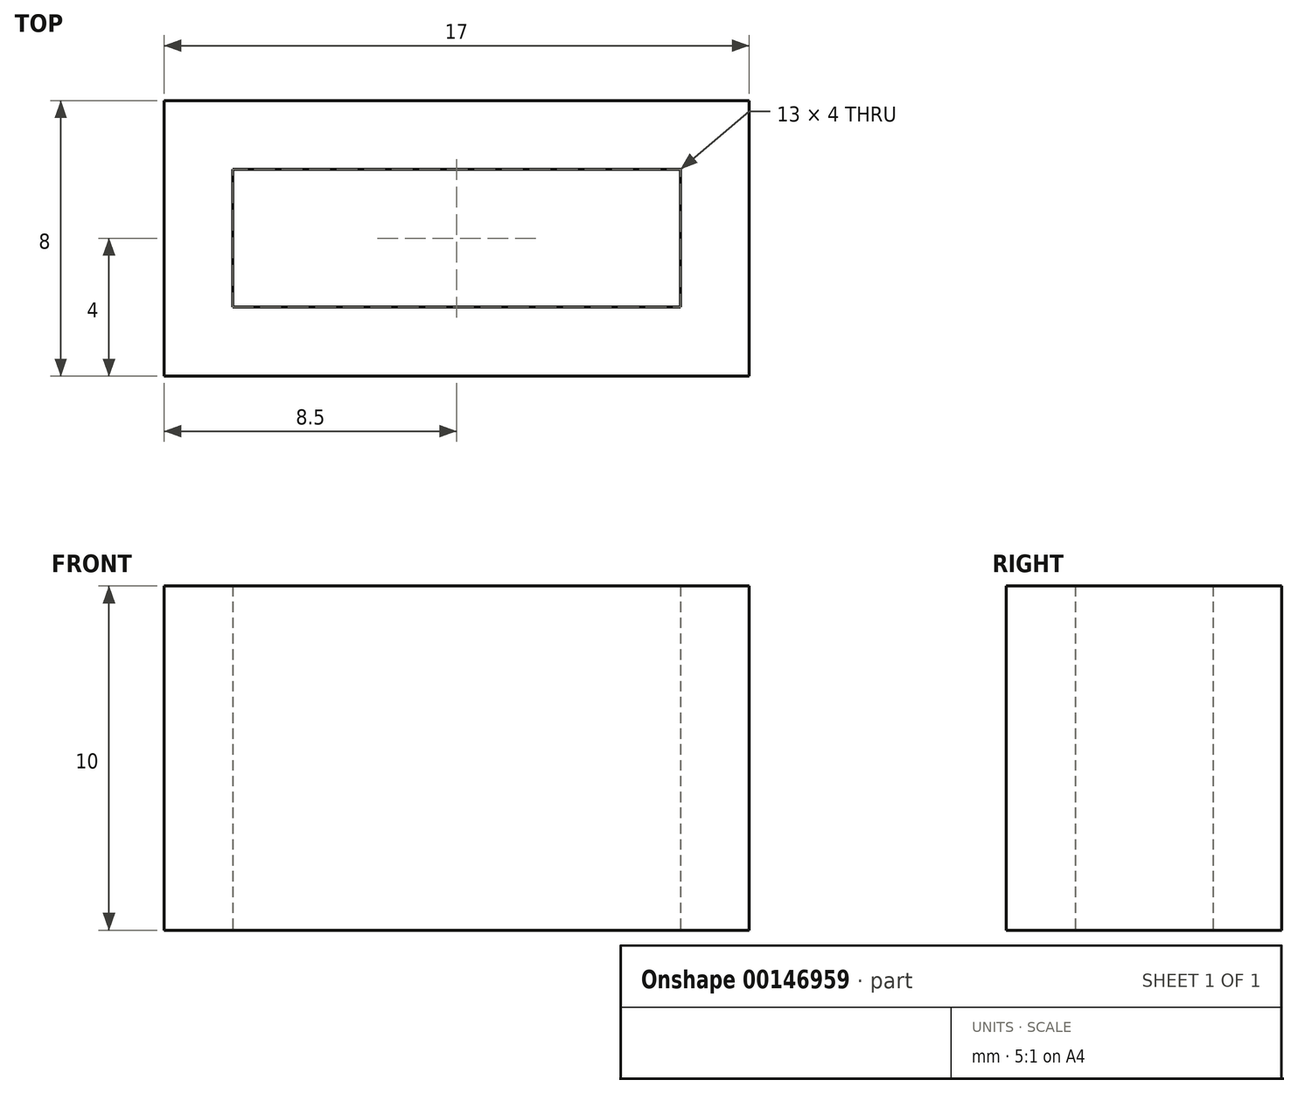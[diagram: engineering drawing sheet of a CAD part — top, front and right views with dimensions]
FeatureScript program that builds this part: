
annotation { "Feature Type Name" : "Feature", "Feature Type Description" : "" }
export const myFeature = defineFeature(function(context is Context, id is Id, definition is map)
    precondition{}
    {
        {
            var Q0;
            Q0=qCreatedBy(makeId("Top.planeOp"),FACE);
            var sketch = newSketch(context, id + "F0", { "sketchPlane" : qUnion([Q0])});
            skLineSegment(sketch, "E0.bottom", {"start": v(0, 0) * mm, "end": v(17, 0) * mm});
            skLineSegment(sketch, "E0.top", {"start": v(0, 8) * mm, "end": v(17, 8) * mm});
            skLineSegment(sketch, "E0.left", {"start": v(0, 0) * mm, "end": v(0, 8) * mm});
            skLineSegment(sketch, "E0.right", {"start": v(17, 0) * mm, "end": v(17, 8) * mm});
            skLineSegment(sketch, "E1.bottom", {"start": v(2, 2) * mm, "end": v(15, 2) * mm});
            skLineSegment(sketch, "E1.top", {"start": v(2, 6) * mm, "end": v(15, 6) * mm});
            skLineSegment(sketch, "E1.left", {"start": v(2, 2) * mm, "end": v(2, 6) * mm});
            skLineSegment(sketch, "E1.right", {"start": v(15, 2) * mm, "end": v(15, 6) * mm});
            skSolve(sketch);
        }
        {
            var Q0;
            Q0 = qSketchRegion(id + "F0", true);
            extrude(context, id + "F1", {"entities" : qUnion([Q0]), "depth" : 10 * mm});
        }
    });
